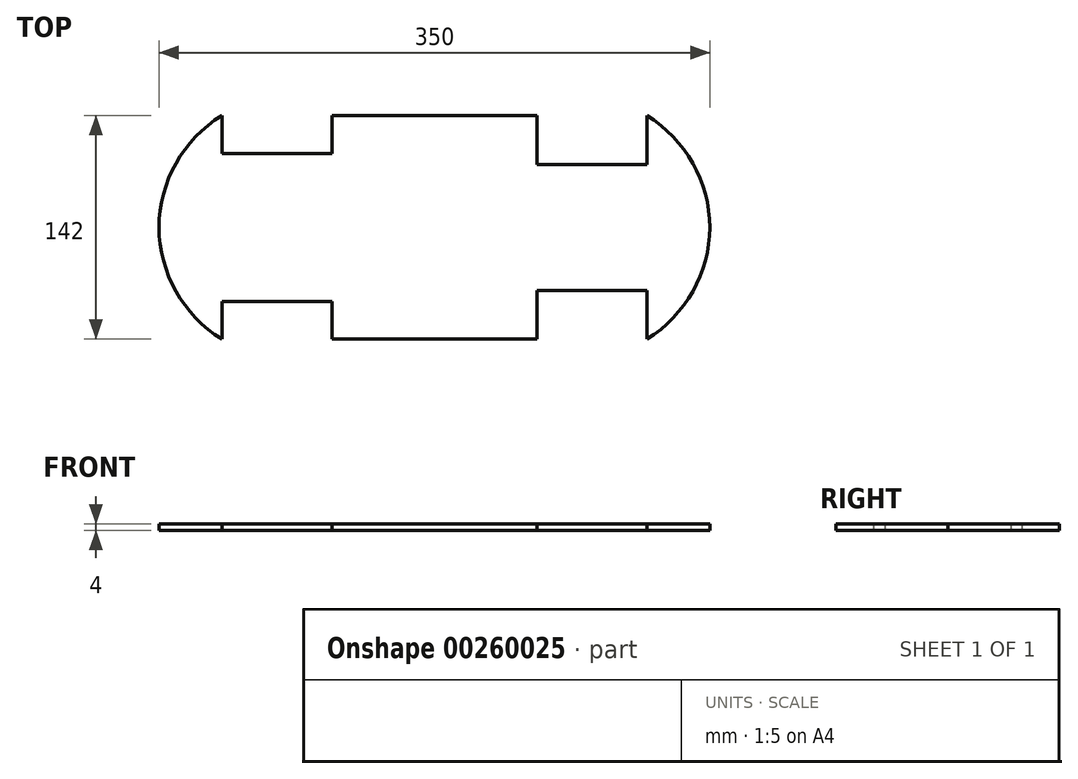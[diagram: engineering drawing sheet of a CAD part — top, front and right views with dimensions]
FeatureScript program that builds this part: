
annotation { "Feature Type Name" : "Feature", "Feature Type Description" : "" }
export const myFeature = defineFeature(function(context is Context, id is Id, definition is map)
    precondition{}
    {
        {
            var Q0;
            Q0=qCreatedBy(makeId("Top.planeOp"),FACE);
            var sketch = newSketch(context, id + "F0", { "sketchPlane" : qUnion([Q0])});
            skLineSegment(sketch, "E0", {"start": v(40, 71.8) * mm, "end": v(40, 47.8) * mm});
            skLineSegment(sketch, "E1", {"start": v(40, 47.8) * mm, "end": v(110, 47.8) * mm});
            skLineSegment(sketch, "E2", {"start": v(110, 47.8) * mm, "end": v(110, 71.8) * mm});
            skLineSegment(sketch, "E3", {"start": v(110, 71.8) * mm, "end": v(240, 71.8) * mm});
            skArc(sketch, "E4.trimOffspring", {"start": v(40, 71.8) * mm, "mid": v(10.67, 41.1) * mm, "end": v(0, 0) * mm});
            skArc(sketch, "E5", {"start": v(350, 0) * mm, "mid": v(339.33, 41.1) * mm, "end": v(310, 71.8) * mm});
            skLineSegment(sketch, "E6", {"start": v(240, 71.8) * mm, "end": v(240, 40.8) * mm});
            skLineSegment(sketch, "E7", {"start": v(240, 40.8) * mm, "end": v(310, 40.8) * mm});
            skLineSegment(sketch, "E8", {"start": v(310, 40.8) * mm, "end": v(310, 71.8) * mm});
            skArc(sketch, "E9.MirrorCS", {"start": v(40, -70.2) * mm, "mid": v(10.67, -39.5) * mm, "end": v(0, 1.6) * mm});
            skLineSegment(sketch, "E10.MirrorCS", {"start": v(110, -70.2) * mm, "end": v(240, -70.2) * mm});
            skArc(sketch, "E11.MirrorCS", {"start": v(350, 1.6) * mm, "mid": v(339.33, -39.5) * mm, "end": v(310, -70.2) * mm});
            skLineSegment(sketch, "E12.MirrorCS", {"start": v(240, -39.2) * mm, "end": v(310, -39.2) * mm});
            skLineSegment(sketch, "E13.MirrorCS", {"start": v(40, -46.2) * mm, "end": v(110, -46.2) * mm});
            skLineSegment(sketch, "E14.MirrorCS", {"start": v(40, -70.2) * mm, "end": v(40, -46.2) * mm});
            skLineSegment(sketch, "E15.MirrorCS", {"start": v(110, -46.2) * mm, "end": v(110, -70.2) * mm});
            skLineSegment(sketch, "E16.MirrorCS", {"start": v(310, -39.2) * mm, "end": v(310, -70.2) * mm});
            skLineSegment(sketch, "E17.MirrorCS", {"start": v(240, -70.2) * mm, "end": v(240, -39.2) * mm});
            skSolve(sketch);
        }
        {
            var Q0;
            Q0=makeQuery(id+"F0.imprint","IMPRINT",FACE,{"disambiguationData":[TD([[makeQuery(id+"F0.imprint","IMPRINT",EDGE,{"derivedFrom":sQuery(id+"F0.wireOp",EDGE,"E0")}),-1.0]])]});
            extrude(context, id + "F1", {"entities" : qUnion([Q0]), "depth" : 4 * mm});
        }
    });
